# Revit family: Mixer tap-Wall_mounted-PRESTO-MURAL NEO FROID 150MM 15SEC-66020
name_source: partatom
category: Plumbing Fixtures
revit_build: Autodesk Revit 2014 (Build: 20130308_1515(x64)
units: mm (PartAtom-declared; Revit-internal decimal feet)

## types (1)
- 66020
    CW Inlet = 13 mm
    Description = PRESTO NEO Single wall-mounted tap (150mm)
    Duration = 7 seconds (± 5 sec.)
    Edition number = 1
    Flow(4-position flow adjustment device) = 3 l/min at 3 bar
    HW Connection = Yes
    HW Inlet = 0 mm  [stored 0 ft]
    Height = 0 mm  [stored 0 ft]
    Lenght = 0 mm  [stored 0 ft]
    Manufacturer = PRESTO LES ROBINETS
    Manufacturer name = Presto
    Material main = Brass
    Material secondary = Chrome
    Model = 66020
    Nominal height = 18900
    Nominal width = 0
    Operating Pressure = 1-5 bar
    Primary Material = Brass-Presto
    Product Guid = 1123172a-c8b6-44d2-8b8d-fb5ab2f158b2
    Product SKU = 66020
    Product data url = https://bimobject.com
    Product family = NEO
    Product group = ROBINET
    QR code = http://bimobject.com
    Secondary Material = Chrome-Presto
    Temp - Resistance(30 minute Thermal Shock) = 75 °C
    Time Flow (± 5 sec) = 15.0 s
    Warranty = 10
    Weight Net (Kg) = 0
    Width = 189 mm  [stored 0.620079 ft]

note: [stored X ft] marks values corroborated as IEEE doubles in the binary element streams (Revit-internal decimal feet)

## geometry (parser evidence)
native form markers: Sweep x5
no freeform markers — native parametric forms only
